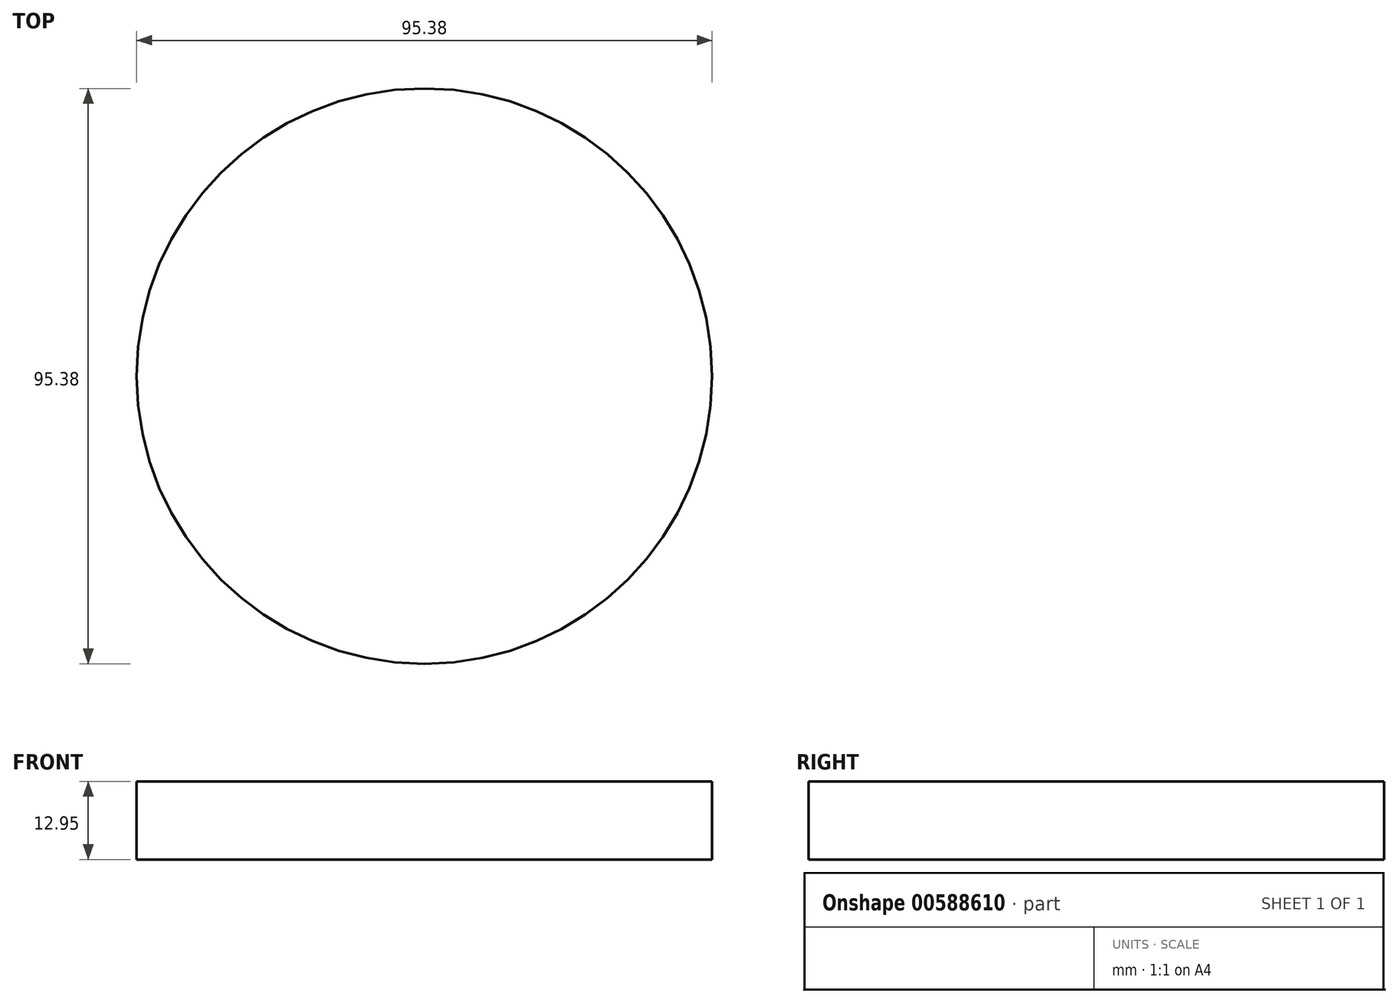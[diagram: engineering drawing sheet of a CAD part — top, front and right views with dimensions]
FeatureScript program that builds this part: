
annotation { "Feature Type Name" : "Feature", "Feature Type Description" : "" }
export const myFeature = defineFeature(function(context is Context, id is Id, definition is map)
    precondition{}
    {
        {
            var Q0;
            Q0=qCreatedBy(makeId("Top.planeOp"),FACE);
            var sketch = newSketch(context, id + "F0", { "sketchPlane" : qUnion([Q0])});
            skCircle(sketch, "E0", {"center": v(0, 0) * mm, "radius": 47.69 * mm});
            skSolve(sketch);
        }
        {
            var Q0;
            Q0 = qSketchRegion(id + "F0", true);
            extrude(context, id + "F1", {"entities" : qUnion([Q0]), "depth" : 12.95 * mm, "offsetDistance" : 25.4 * mm});
        }
    });
